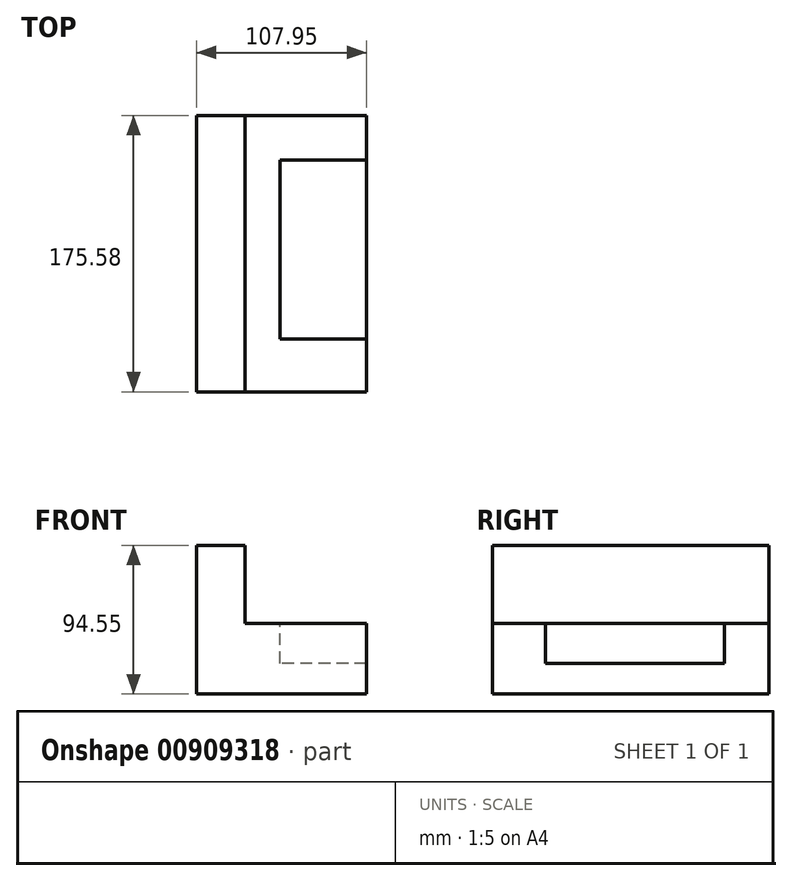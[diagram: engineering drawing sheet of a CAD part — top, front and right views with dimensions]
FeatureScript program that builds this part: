
annotation { "Feature Type Name" : "Feature", "Feature Type Description" : "" }
export const myFeature = defineFeature(function(context is Context, id is Id, definition is map)
    precondition{}
    {
        {
            var Q0;
            Q0=qCreatedBy(makeId("Right.planeOp"),FACE);
            var sketch = newSketch(context, id + "F0", { "sketchPlane" : qUnion([Q0])});
            skLineSegment(sketch, "E0.bottom", {"start": v(-82.28, 51.68) * mm, "end": v(93.3, 51.68) * mm});
            skLineSegment(sketch, "E0.top", {"start": v(-82.28, -42.87) * mm, "end": v(93.3, -42.87) * mm});
            skLineSegment(sketch, "E0.left", {"start": v(-82.28, 51.68) * mm, "end": v(-82.28, -42.87) * mm});
            skLineSegment(sketch, "E0.right", {"start": v(93.3, 51.68) * mm, "end": v(93.3, -42.87) * mm});
            skSolve(sketch);
        }
        {
            var Q0;
            Q0=makeQuery(id+"F0.imprint","IMPRINT",FACE,{"disambiguationData":[TD([[makeQuery(id+"F0.imprint","IMPRINT",EDGE,{"derivedFrom":sQuery(id+"F0.wireOp",EDGE,"E0.bottom")}),-1.0]])]});
            extrude(context, id + "F1", {"entities" : qUnion([Q0]), "depth" : 107.95 * mm, "offsetDistance" : 25.4 * mm});
        }
        {
            var Q0;
            Q0=makeQuery(id+"F1.opExtrude","SWEPT_FACE",FACE,{"disambiguationData":[OSD([sQuery(id+"F0.wireOp",EDGE,"E0.bottom")])]});
            var sketch = newSketch(context, id + "F2", { "sketchPlane" : qUnion([Q0])});
            skLineSegment(sketch, "E1", {"start": v(30.87, -82.28) * mm, "end": v(30.87, 93.3) * mm});
            skSolve(sketch);
        }
        {
            var Q0;
            {var subQ0=sQuery(id+"F2.wireOp",EDGE,"E1");Q0=makeQuery(id+"F2.imprint","IMPRINT",FACE,{"disambiguationData":[TD([[makeQuery(id+"F2.imprint","IMPRINT",EDGE,{"derivedFrom":subQ0}),-1.0]])]});}
            extrude(context, id + "F3", {"entities" : qUnion([Q0]), "operationType" : NewBodyOperationType.REMOVE, "oppositeDirection" : true, "depth" : 49.53 * mm, "offsetDistance" : 25.4 * mm});
        }
        {
            var Q0;
            Q0=makeQuery(id+"F3.boolean.opBoolean","COPY",FACE,{"derivedFrom":makeQuery(id+"F3.opExtrude","CAP_FACE",FACE,{"disambiguationData":[OSD([sQuery(id+"F0.wireOp",EDGE,"E0.bottom"),sQuery(id+"F0.wireOp",EDGE,"E0.left"),sQuery(id+"F0.wireOp",EDGE,"E0.right"),sQuery(id+"F2.wireOp",EDGE,"E1")])],"isStart":false})});
            var sketch = newSketch(context, id + "F4", { "sketchPlane" : qUnion([Q0])});
            skLineSegment(sketch, "E2.bottom", {"start": v(107.95, -48.69) * mm, "end": v(52.95, -48.69) * mm});
            skLineSegment(sketch, "E2.top", {"start": v(107.95, 64.95) * mm, "end": v(52.95, 64.95) * mm});
            skLineSegment(sketch, "E2.left", {"start": v(107.95, -48.69) * mm, "end": v(107.95, 64.95) * mm});
            skLineSegment(sketch, "E2.right", {"start": v(52.95, -48.69) * mm, "end": v(52.95, 64.95) * mm});
            skSolve(sketch);
        }
        {
            var Q0;
            Q0=makeQuery(id+"F4.imprint","IMPRINT",FACE,{"disambiguationData":[TD([[makeQuery(id+"F4.imprint","IMPRINT",EDGE,{"derivedFrom":sQuery(id+"F4.wireOp",EDGE,"E2.bottom")}),-1.0]])]});
            extrude(context, id + "F5", {"entities" : qUnion([Q0]), "operationType" : NewBodyOperationType.REMOVE, "oppositeDirection" : true, "depth" : 25.4 * mm, "offsetDistance" : 25.4 * mm});
        }
    });
